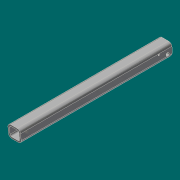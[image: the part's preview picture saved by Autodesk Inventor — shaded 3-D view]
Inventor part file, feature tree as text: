
AUTODESK INVENTOR PART (.ipt)
format: ipt  version: 2017 (Build 210142000, 142)  size: 179,200 bytes
history: native  units: mm (DEFAULTED — no unit token found)
features: sketch x5, other x3, hole x2, extrude x1, plane x1
ambient origin geometry x8: Origin, YZ Plane, XZ Plane, XY Plane, X Axis, Y Axis, Z Axis, Center Point
bodies: Solid1 (feature_tree), Body (feature_tree)
feature tree (12):
  other  "Driven Length"
  other  "Start plane"
  other  "End plane"
  extrude  "Extrusion2"  TaperAngle=0.0deg  [1 undecoded]
  hole  "Hole1"  [1 undecoded]
  hole  "Hole2"  [1 undecoded]
  sketch  "Sketch"  dims[d15=25.4mm d16=25.4mm d17=12.7mm d18=90.0deg d19=609.6mm d20=0.872665mm d21=25.4mm d22=0.0mm d23=19.05mm d24=25.4mm d25=25.4mm d26=12.7mm d27=19.05mm d28=9.525mm d29=6.35mm d30=14.3117mm d31=25.4mm d32=20.594885mm d33=53.975mm d34=9.525mm d35=6.35mm d36=19.05mm d37=9.525mm d38=6.35mm d39=14.3117mm d40=25.4mm d41=20.594885mm]
  sketch  "Sketch3"  dims[d3=609.6mm d4=0.0mm]
  plane  "Work Plane3"
  sketch  "Sketch4"  dims[d10=50.8mm d11=50.8mm]
  sketch  "Sketch5"  dims[d12=6.35mm d13=-0.0mm]
  sketch  "Sketch6"  dims[d14=609.6mm]
note: 3 required parameter values undecoded (feature->parameter linkage not recoverable at this tier; creation-order binding heuristic only, values carry confidence <= 0.55)
